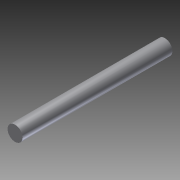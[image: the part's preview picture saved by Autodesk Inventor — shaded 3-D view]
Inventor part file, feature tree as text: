
AUTODESK INVENTOR PART (.ipt)
format: ipt  version: 2012 (Build 160160000, 160)  size: 69,120 bytes
history: native  units: in
note: dims shown in document units (in); Inventor stores cm internally (conversion verified against a paired STEP export)
features: extrude x1, sketch x1
ambient origin geometry x8: Origin, YZ Plane, XZ Plane, XY Plane, X Axis, Y Axis, Z Axis, Center Point
bodies: Solid1 (feature_tree)
feature tree (2):
  extrude  "Extrusion1"  Depth=10.0in TaperAngle=0.0deg
  sketch  "Sketch1"  dims[d0=1.0in d1=10.0in d2=0.0in]
